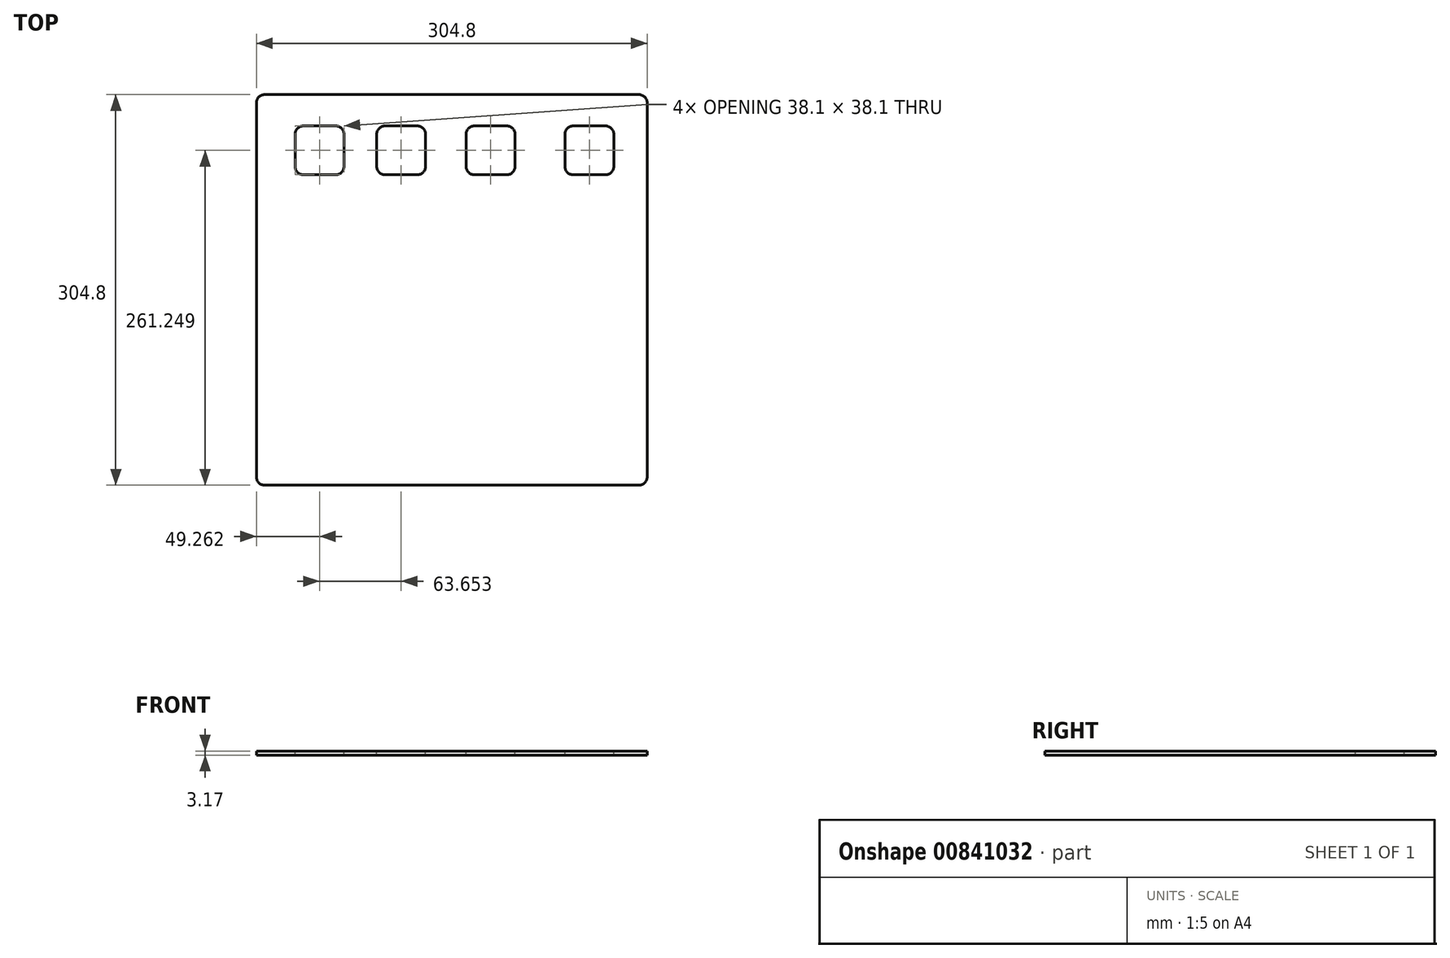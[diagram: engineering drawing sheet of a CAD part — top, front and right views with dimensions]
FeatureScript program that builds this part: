
annotation { "Feature Type Name" : "Feature", "Feature Type Description" : "" }
export const myFeature = defineFeature(function(context is Context, id is Id, definition is map)
    precondition{}
    {
        {
            var Q0;
            Q0=qCreatedBy(makeId("Top.planeOp"),FACE);
            var sketch = newSketch(context, id + "F0", { "sketchPlane" : qUnion([Q0])});
            skLineSegment(sketch, "E0.bottom", {"start": v(146.05, 152.4) * mm, "end": v(-146.05, 152.4) * mm});
            skLineSegment(sketch, "E0.top", {"start": v(146.05, -152.4) * mm, "end": v(-146.05, -152.4) * mm});
            skLineSegment(sketch, "E0.left", {"start": v(152.4, 146.05) * mm, "end": v(152.4, -146.05) * mm});
            skLineSegment(sketch, "E0.right", {"start": v(-152.4, 146.05) * mm, "end": v(-152.4, -146.05) * mm});
            skPoint(sketch, "E0.middle", {"position": v(0, 0) * mm});
            skPoint(sketch, "E1.visualSharp", {"position": v(-152.4, 152.4) * mm});
            skArc(sketch, "E1.filletArc", {"start": v(-146.05, 152.4) * mm, "mid": v(-150.54, 150.54) * mm, "end": v(-152.4, 146.05) * mm});
            skPoint(sketch, "E2.visualSharp", {"position": v(152.4, 152.4) * mm});
            skArc(sketch, "E2.filletArc", {"start": v(152.4, 146.05) * mm, "mid": v(150.54, 150.54) * mm, "end": v(146.05, 152.4) * mm});
            skPoint(sketch, "E3.visualSharp", {"position": v(-152.4, -152.4) * mm});
            skArc(sketch, "E3.filletArc", {"start": v(-152.4, -146.05) * mm, "mid": v(-150.54, -150.54) * mm, "end": v(-146.05, -152.4) * mm});
            skPoint(sketch, "E4.visualSharp", {"position": v(152.4, -152.4) * mm});
            skArc(sketch, "E4.filletArc", {"start": v(146.05, -152.4) * mm, "mid": v(150.54, -150.54) * mm, "end": v(152.4, -146.05) * mm});
            skSolve(sketch);
        }
        {
            var Q0;
            Q0 = qSketchRegion(id + "F0", true);
            extrude(context, id + "F1", {"entities" : qUnion([Q0]), "depth" : 3.17 * mm, "offsetDistance" : 25.4 * mm});
        }
        {
            var Q0;
            Q0=makeQuery(id+"F1.opExtrude","CAP_FACE",FACE,{"disambiguationData":[OSD([sQuery(id+"F0.wireOp",EDGE,"E0.bottom"),sQuery(id+"F0.wireOp",EDGE,"E0.top"),sQuery(id+"F0.wireOp",EDGE,"E0.left"),sQuery(id+"F0.wireOp",EDGE,"E0.right"),sQuery(id+"F0.wireOp",EDGE,"E1.filletArc"),sQuery(id+"F0.wireOp",EDGE,"E2.filletArc"),sQuery(id+"F0.wireOp",EDGE,"E3.filletArc"),sQuery(id+"F0.wireOp",EDGE,"E4.filletArc")])],"isStart":false});
            var sketch = newSketch(context, id + "F2", { "sketchPlane" : qUnion([Q0])});
            skLineSegment(sketch, "E5.bottom", {"start": v(-90.44, 89.8) * mm, "end": v(-115.84, 89.8) * mm});
            skLineSegment(sketch, "E5.top", {"start": v(-90.44, 127.9) * mm, "end": v(-115.84, 127.9) * mm});
            skLineSegment(sketch, "E5.left", {"start": v(-84.09, 96.15) * mm, "end": v(-84.09, 121.55) * mm});
            skLineSegment(sketch, "E5.right", {"start": v(-122.19, 96.15) * mm, "end": v(-122.19, 121.55) * mm});
            skPoint(sketch, "E5.middle", {"position": v(-103.14, 108.85) * mm});
            skLineSegment(sketch, "E6.bottom", {"start": v(-26.79, 89.8) * mm, "end": v(-52.19, 89.8) * mm});
            skLineSegment(sketch, "E6.top", {"start": v(-26.79, 127.9) * mm, "end": v(-52.19, 127.9) * mm});
            skLineSegment(sketch, "E6.left", {"start": v(-20.44, 96.15) * mm, "end": v(-20.44, 121.55) * mm});
            skLineSegment(sketch, "E6.right", {"start": v(-58.54, 96.15) * mm, "end": v(-58.54, 121.55) * mm});
            skPoint(sketch, "E6.middle", {"position": v(-39.49, 108.85) * mm});
            skLineSegment(sketch, "E7.bottom", {"start": v(120, 89.8) * mm, "end": v(94.6, 89.8) * mm});
            skLineSegment(sketch, "E7.top", {"start": v(120, 127.9) * mm, "end": v(94.6, 127.9) * mm});
            skLineSegment(sketch, "E7.left", {"start": v(126.35, 96.15) * mm, "end": v(126.35, 121.55) * mm});
            skLineSegment(sketch, "E7.right", {"start": v(88.25, 96.15) * mm, "end": v(88.25, 121.55) * mm});
            skPoint(sketch, "E7.middle", {"position": v(107.3, 108.85) * mm});
            skLineSegment(sketch, "E8.bottom", {"start": v(42.98, 89.8) * mm, "end": v(17.58, 89.8) * mm});
            skLineSegment(sketch, "E8.top", {"start": v(42.98, 127.9) * mm, "end": v(17.58, 127.9) * mm});
            skLineSegment(sketch, "E8.left", {"start": v(49.33, 96.15) * mm, "end": v(49.33, 121.55) * mm});
            skLineSegment(sketch, "E8.right", {"start": v(11.23, 96.15) * mm, "end": v(11.23, 121.55) * mm});
            skPoint(sketch, "E8.middle", {"position": v(30.28, 108.85) * mm});
            skPoint(sketch, "E9.visualSharp", {"position": v(-122.19, 127.9) * mm});
            skArc(sketch, "E9.filletArc", {"start": v(-115.84, 127.9) * mm, "mid": v(-120.33, 126.04) * mm, "end": v(-122.19, 121.55) * mm});
            skPoint(sketch, "E10.visualSharp", {"position": v(-122.19, 89.8) * mm});
            skArc(sketch, "E10.filletArc", {"start": v(-122.19, 96.15) * mm, "mid": v(-120.33, 91.66) * mm, "end": v(-115.84, 89.8) * mm});
            skPoint(sketch, "E11.visualSharp", {"position": v(-84.09, 89.8) * mm});
            skArc(sketch, "E11.filletArc", {"start": v(-90.44, 89.8) * mm, "mid": v(-85.95, 91.66) * mm, "end": v(-84.09, 96.15) * mm});
            skPoint(sketch, "E12.visualSharp", {"position": v(-84.09, 127.9) * mm});
            skArc(sketch, "E12.filletArc", {"start": v(-84.09, 121.55) * mm, "mid": v(-85.95, 126.04) * mm, "end": v(-90.44, 127.9) * mm});
            skPoint(sketch, "E13.visualSharp", {"position": v(-58.54, 127.9) * mm});
            skArc(sketch, "E13.filletArc", {"start": v(-52.19, 127.9) * mm, "mid": v(-56.68, 126.04) * mm, "end": v(-58.54, 121.55) * mm});
            skPoint(sketch, "E14.visualSharp", {"position": v(-58.54, 89.8) * mm});
            skArc(sketch, "E14.filletArc", {"start": v(-58.54, 96.15) * mm, "mid": v(-56.68, 91.66) * mm, "end": v(-52.19, 89.8) * mm});
            skPoint(sketch, "E15.visualSharp", {"position": v(-20.44, 89.8) * mm});
            skArc(sketch, "E15.filletArc", {"start": v(-26.79, 89.8) * mm, "mid": v(-22.3, 91.66) * mm, "end": v(-20.44, 96.15) * mm});
            skPoint(sketch, "E16.visualSharp", {"position": v(-20.44, 127.9) * mm});
            skArc(sketch, "E16.filletArc", {"start": v(-20.44, 121.55) * mm, "mid": v(-22.3, 126.04) * mm, "end": v(-26.79, 127.9) * mm});
            skPoint(sketch, "E17.visualSharp", {"position": v(11.23, 127.9) * mm});
            skArc(sketch, "E17.filletArc", {"start": v(17.58, 127.9) * mm, "mid": v(13.09, 126.04) * mm, "end": v(11.23, 121.55) * mm});
            skPoint(sketch, "E18.visualSharp", {"position": v(49.33, 127.9) * mm});
            skArc(sketch, "E18.filletArc", {"start": v(49.33, 121.55) * mm, "mid": v(47.47, 126.04) * mm, "end": v(42.98, 127.9) * mm});
            skPoint(sketch, "E19.visualSharp", {"position": v(11.23, 89.8) * mm});
            skArc(sketch, "E19.filletArc", {"start": v(11.23, 96.15) * mm, "mid": v(13.09, 91.66) * mm, "end": v(17.58, 89.8) * mm});
            skPoint(sketch, "E20.visualSharp", {"position": v(49.33, 89.8) * mm});
            skArc(sketch, "E20.filletArc", {"start": v(42.98, 89.8) * mm, "mid": v(47.47, 91.66) * mm, "end": v(49.33, 96.15) * mm});
            skPoint(sketch, "E21.visualSharp", {"position": v(88.25, 89.8) * mm});
            skArc(sketch, "E21.filletArc", {"start": v(88.25, 96.15) * mm, "mid": v(90.11, 91.66) * mm, "end": v(94.6, 89.8) * mm});
            skPoint(sketch, "E22.visualSharp", {"position": v(88.25, 127.9) * mm});
            skArc(sketch, "E22.filletArc", {"start": v(94.6, 127.9) * mm, "mid": v(90.11, 126.04) * mm, "end": v(88.25, 121.55) * mm});
            skPoint(sketch, "E23.visualSharp", {"position": v(126.35, 127.9) * mm});
            skArc(sketch, "E23.filletArc", {"start": v(126.35, 121.55) * mm, "mid": v(124.5, 126.04) * mm, "end": v(120, 127.9) * mm});
            skPoint(sketch, "E24.visualSharp", {"position": v(126.35, 89.8) * mm});
            skArc(sketch, "E24.filletArc", {"start": v(120, 89.8) * mm, "mid": v(124.5, 91.66) * mm, "end": v(126.35, 96.15) * mm});
            skLineSegment(sketch, "E25.bottom", {"start": v(-77.74, 83.45) * mm, "end": v(-128.54, 83.45) * mm, "construction": true});
            skLineSegment(sketch, "E25.top", {"start": v(-77.74, 134.25) * mm, "end": v(-128.54, 134.25) * mm, "construction": true});
            skLineSegment(sketch, "E25.left", {"start": v(-77.74, 83.45) * mm, "end": v(-77.74, 134.25) * mm, "construction": true});
            skLineSegment(sketch, "E25.right", {"start": v(-128.54, 83.45) * mm, "end": v(-128.54, 134.25) * mm, "construction": true});
            skSolve(sketch);
        }
        {
            var Q0;
            Q0 = qSketchRegion(id + "F2", true);
            extrude(context, id + "F3", {"entities" : qUnion([Q0]), "operationType" : NewBodyOperationType.REMOVE, "endBound" : BoundingType.UP_TO_NEXT, "oppositeDirection" : true, "depth" : 25.4 * mm, "offsetDistance" : 25.4 * mm});
        }
    });
